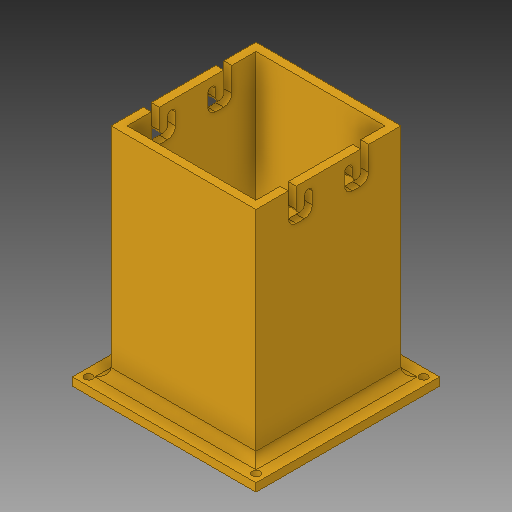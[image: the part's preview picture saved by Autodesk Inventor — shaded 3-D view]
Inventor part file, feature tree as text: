
AUTODESK INVENTOR PART (.ipt)
format: ipt  version: 2019 (Build 230136000, 136)  size: 249,344 bytes
history: native  units: in
note: dims shown in document units (in); Inventor stores cm internally (conversion verified against a paired STEP export)
features: extrude x4, sketch x3, plane x3, fillet x3, mirror x2, hole x1, projected_geometry x1
ambient origin geometry x8: Origin, YZ Plane, XZ Plane, XY Plane, X Axis, Y Axis, Z Axis, Center Point
bodies: Solid1 (feature_tree)
feature tree (17):
  sketch  "Sketch1"  dims[d6=3.5in d7=0.0in d10=0.125in]
  extrude  "Extrusion1"  Depth=0.125in
  sketch  "Sketch2"  dims[d11=0.5in d12=0.375in]
  plane  "Work Plane1"
  plane  "Work Plane2"
  extrude  "Extrusion5"  Depth=0.375in
  extrude  "Extrusion6"  Depth=0.125in
  hole  "Hole1"  [1 undecoded]
  fillet  "Fillet2"  Radius=0.5in
  extrude  "Extrusion7"  Depth=2.0in
  fillet  "Fillet4"  Radius=2.0in
  fillet  "Fillet5"  Radius=0.25in
  mirror  "Mirror3"
  mirror  "Mirror4"
  sketch  "Sketch3"  dims[d13=0.125in d14=0.125in d15=0.125in d16=0.5in d20=2.0in d21=2.0in d22=0.25in d23=0.125in d24=0.125in d25=0.125in d26=0.125in d27=0.25in d28=0.25in d29=0.25in d32=0.125in d33=0.0in d34=0.3in d35=0.3in d36=0.3in d37=0.3in d38=0.125in d39=0.0in d40=0.125in d41=0.125in d42=0.125in d43=0.125in d44=0.125in d45=0.125in d46=0.125in d47=0.125in d48=0.125in d49=0.75in d50=0.375in d51=0.25in d52=0.5635in d53=1.0in d54=0.8108in d55=0.125in d56=0.3in d57=0.375in d58=0.375in d59=1.0in d60=0.0in d62=0.125in d63=0.0625in d64=0.125in]
  projected_geometry  "Projected Loop1"
  plane  "Work Plane4"
note: 1 required parameter value undecoded (feature->parameter linkage not recoverable at this tier; creation-order binding heuristic only, values carry confidence <= 0.55)
